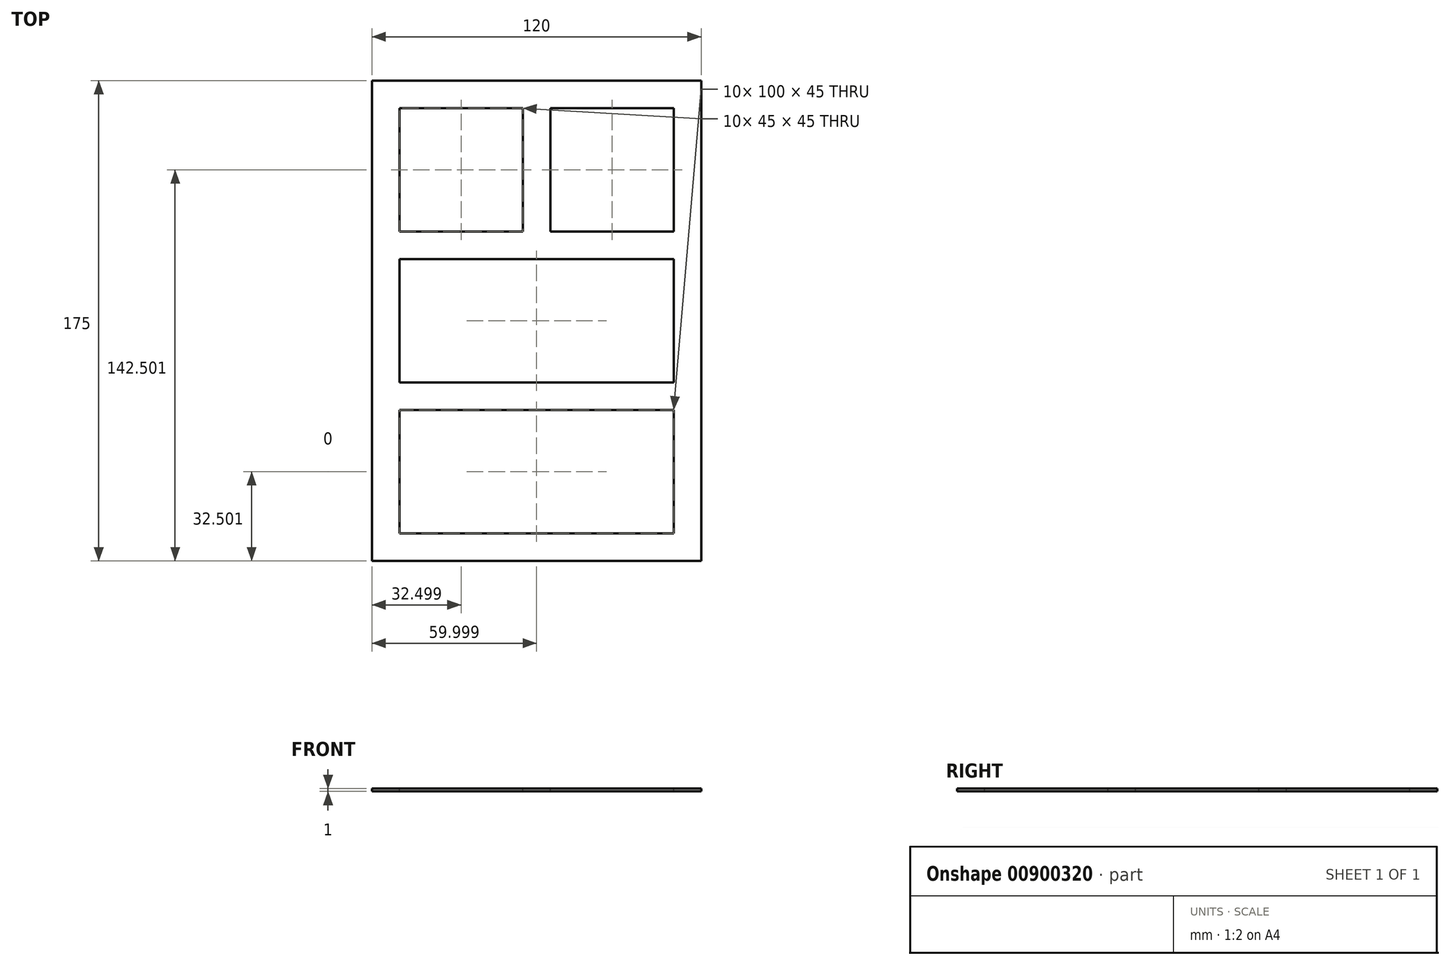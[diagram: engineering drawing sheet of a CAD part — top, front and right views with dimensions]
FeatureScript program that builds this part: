
annotation { "Feature Type Name" : "Feature", "Feature Type Description" : "" }
export const myFeature = defineFeature(function(context is Context, id is Id, definition is map)
    precondition{}
    {
        {
            var Q0;
            Q0=qCreatedBy(makeId("Top.planeOp"),FACE);
            var sketch = newSketch(context, id + "F0", { "sketchPlane" : qUnion([Q0])});
            skLineSegment(sketch, "E0.bottom", {"start": v(-60.8, 100.36) * mm, "end": v(59.2, 100.36) * mm});
            skLineSegment(sketch, "E0.top", {"start": v(-60.8, -74.64) * mm, "end": v(59.2, -74.64) * mm});
            skLineSegment(sketch, "E0.left", {"start": v(-60.8, 100.36) * mm, "end": v(-60.8, -74.64) * mm});
            skLineSegment(sketch, "E0.right", {"start": v(59.2, 100.36) * mm, "end": v(59.2, -74.64) * mm});
            skLineSegment(sketch, "E1.bottom", {"start": v(-50.8, 90.36) * mm, "end": v(-5.8, 90.36) * mm});
            skLineSegment(sketch, "E1.top", {"start": v(-50.8, 45.36) * mm, "end": v(-5.8, 45.36) * mm});
            skLineSegment(sketch, "E1.left", {"start": v(-50.8, 90.36) * mm, "end": v(-50.8, 45.36) * mm});
            skLineSegment(sketch, "E1.right", {"start": v(-5.8, 90.36) * mm, "end": v(-5.8, 45.36) * mm});
            skLineSegment(sketch, "E2.bottom", {"start": v(-50.8, 35.36) * mm, "end": v(49.2, 35.36) * mm});
            skLineSegment(sketch, "E2.top", {"start": v(-50.8, -9.64) * mm, "end": v(49.2, -9.64) * mm});
            skLineSegment(sketch, "E2.left", {"start": v(-50.8, 35.36) * mm, "end": v(-50.8, -9.64) * mm});
            skLineSegment(sketch, "E2.right", {"start": v(49.2, 35.36) * mm, "end": v(49.2, -9.64) * mm});
            skLineSegment(sketch, "E3.bottom", {"start": v(4.2, 90.36) * mm, "end": v(49.2, 90.36) * mm});
            skLineSegment(sketch, "E3.top", {"start": v(4.2, 45.36) * mm, "end": v(49.2, 45.36) * mm});
            skLineSegment(sketch, "E3.left", {"start": v(4.2, 90.36) * mm, "end": v(4.2, 45.36) * mm});
            skLineSegment(sketch, "E3.right", {"start": v(49.2, 90.36) * mm, "end": v(49.2, 45.36) * mm});
            skLineSegment(sketch, "E4.bottom", {"start": v(-50.8, -19.64) * mm, "end": v(49.2, -19.64) * mm});
            skLineSegment(sketch, "E4.top", {"start": v(-50.8, -64.64) * mm, "end": v(49.2, -64.64) * mm});
            skLineSegment(sketch, "E4.left", {"start": v(-50.8, -19.64) * mm, "end": v(-50.8, -64.64) * mm});
            skLineSegment(sketch, "E4.right", {"start": v(49.2, -19.64) * mm, "end": v(49.2, -64.64) * mm});
            skSolve(sketch);
        }
        {
            var Q0;
            Q0=makeQuery(id+"F0.imprint","IMPRINT",FACE,{"disambiguationData":[TD([[makeQuery(id+"F0.imprint","IMPRINT",EDGE,{"derivedFrom":sQuery(id+"F0.wireOp",EDGE,"E0.bottom")}),-1.0]])]});
            extrude(context, id + "F1", {"entities" : qUnion([Q0]), "oppositeDirection" : true, "depth" : 1 * mm, "offsetDistance" : 25 * mm});
        }
    });
